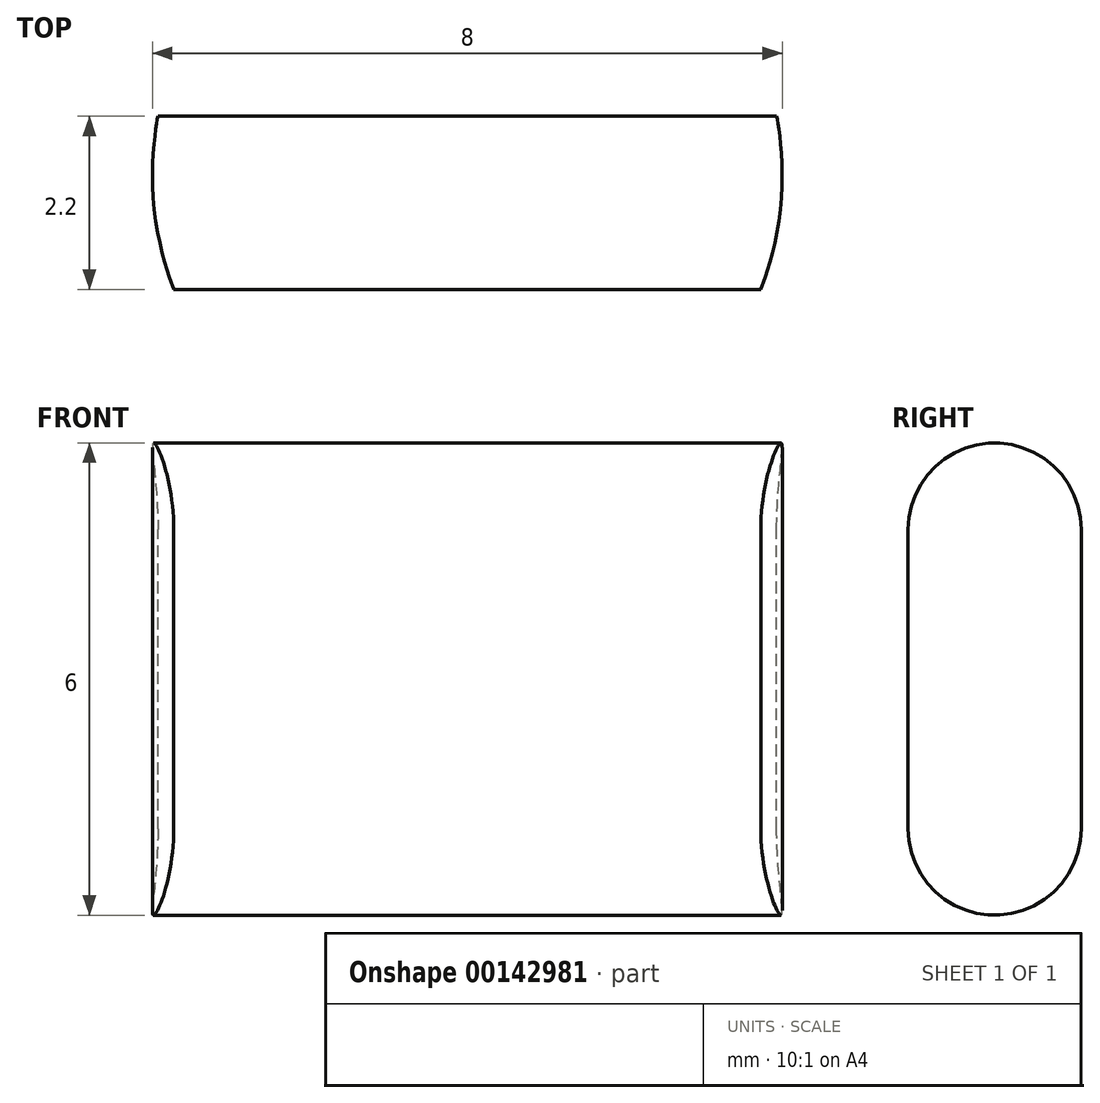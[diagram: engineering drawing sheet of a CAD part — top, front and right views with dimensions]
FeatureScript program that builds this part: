
annotation { "Feature Type Name" : "Feature", "Feature Type Description" : "" }
export const myFeature = defineFeature(function(context is Context, id is Id, definition is map)
    precondition{}
    {
        {
            var Q0;
            Q0=qCreatedBy(makeId("Right.planeOp"),FACE);
            var sketch = newSketch(context, id + "F0", { "sketchPlane" : qUnion([Q0])});
            skLineSegment(sketch, "E0.bottom", {"start": v(0.75, -1.8) * mm, "end": v(-1.45, -1.8) * mm, "construction": true});
            skLineSegment(sketch, "E0.top", {"start": v(0.75, 2) * mm, "end": v(-1.45, 2) * mm, "construction": true});
            skLineSegment(sketch, "E0.left", {"start": v(0.75, -1.8) * mm, "end": v(0.75, 2) * mm});
            skLineSegment(sketch, "E0.right", {"start": v(-1.45, -1.8) * mm, "end": v(-1.45, 2) * mm});
            skArc(sketch, "E1", {"start": v(-1.45, 2) * mm, "mid": v(-0.35, 3.1) * mm, "end": v(0.75, 2) * mm});
            skArc(sketch, "E2", {"start": v(-1.45, -1.8) * mm, "mid": v(-0.35, -2.9) * mm, "end": v(0.75, -1.8) * mm});
            skSolve(sketch);
        }
        {
            var Q0;
            Q0 = qSketchRegion(id + "F0", true);
            extrude(context, id + "F1", {"entities" : qUnion([Q0]), "endBound" : BoundingType.SYMMETRIC, "depth" : 10 * mm});
        }
        {
            var Q0;
            Q0=qCreatedBy(makeId("Top.planeOp"),FACE);
            var sketch = newSketch(context, id + "F2", { "sketchPlane" : qUnion([Q0])});
            skCircle(sketch, "E3", {"center": v(0, 0) * mm, "radius": 4 * mm});
            skLineSegment(sketch, "E4.bottom", {"start": v(-10, -10) * mm, "end": v(10, -10) * mm});
            skLineSegment(sketch, "E4.top", {"start": v(-10, 10) * mm, "end": v(10, 10) * mm});
            skLineSegment(sketch, "E4.left", {"start": v(-10, -10) * mm, "end": v(-10, 10) * mm});
            skLineSegment(sketch, "E4.right", {"start": v(10, -10) * mm, "end": v(10, 10) * mm});
            skSolve(sketch);
        }
        {
            var Q0;
            Q0 = qSketchRegion(id + "F2", true);
            extrude(context, id + "F3", {"entities" : qUnion([Q0]), "operationType" : NewBodyOperationType.REMOVE, "endBound" : BoundingType.SYMMETRIC, "oppositeDirection" : true, "depth" : 25 * mm});
        }
    });
